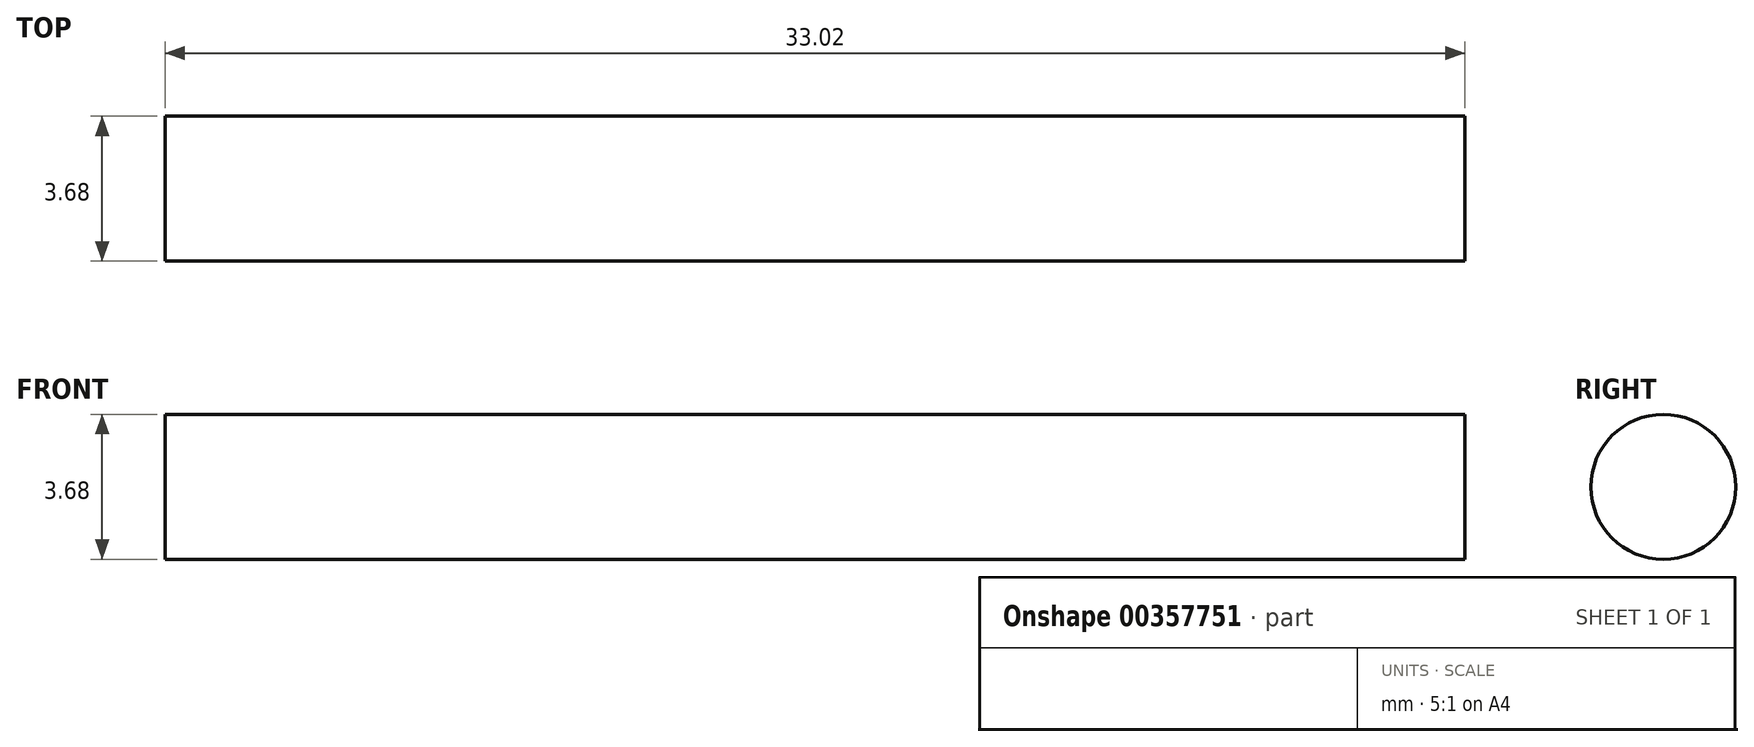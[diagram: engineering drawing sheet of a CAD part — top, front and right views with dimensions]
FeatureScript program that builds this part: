
annotation { "Feature Type Name" : "Feature", "Feature Type Description" : "" }
export const myFeature = defineFeature(function(context is Context, id is Id, definition is map)
    precondition{}
    {
        {
            var Q0;
            Q0=qCreatedBy(makeId("Right.planeOp"),FACE);
            var sketch = newSketch(context, id + "F0", { "sketchPlane" : qUnion([Q0])});
            skCircle(sketch, "E0", {"center": v(0, 0) * mm, "radius": 1.84 * mm});
            skSolve(sketch);
        }
        {
            var Q0;
            Q0=makeQuery(id+"F0.imprint","IMPRINT",FACE,{"disambiguationData":[TD([[makeQuery(id+"F0.imprint","IMPRINT",EDGE,{"derivedFrom":sQuery(id+"F0.wireOp",EDGE,"E0")}),1.0]])]});
            extrude(context, id + "F1", {"entities" : qUnion([Q0]), "depth" : 16.5 * mm, "hasSecondDirection" : true, "secondDirectionOppositeDirection" : true, "secondDirectionDepth" : 16.5 * mm});
        }
    });
